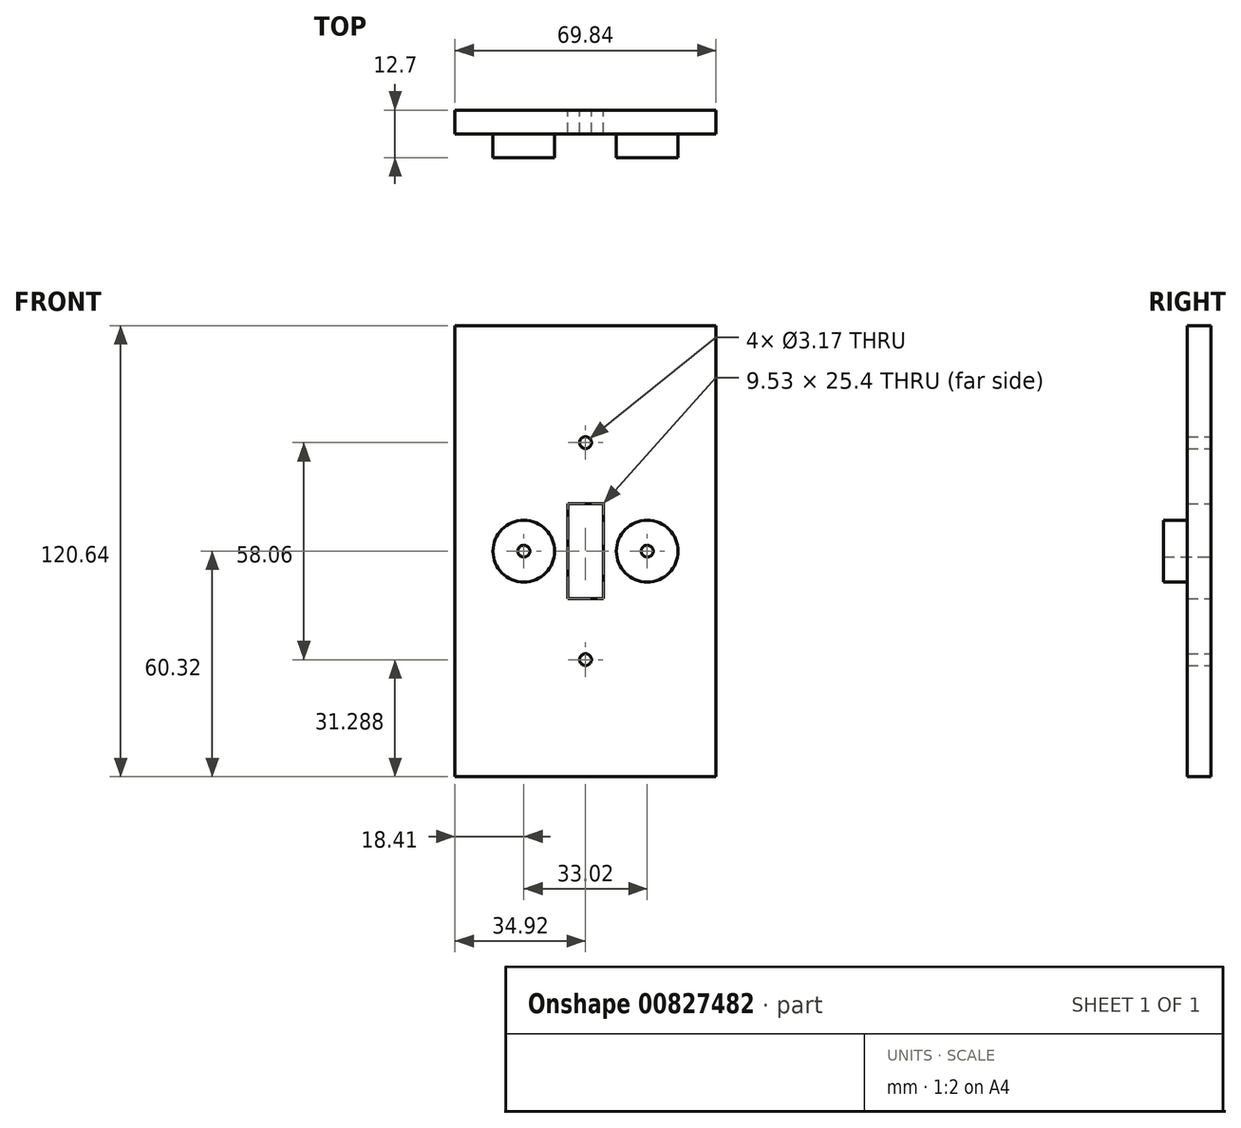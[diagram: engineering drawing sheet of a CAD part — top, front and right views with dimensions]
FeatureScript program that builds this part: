
annotation { "Feature Type Name" : "Feature", "Feature Type Description" : "" }
export const myFeature = defineFeature(function(context is Context, id is Id, definition is map)
    precondition{}
    {
        {
            var Q0;
            Q0=qCreatedBy(makeId("Front.planeOp"),FACE);
            var sketch = newSketch(context, id + "F0", { "sketchPlane" : qUnion([Q0])});
            skLineSegment(sketch, "E0.bottom", {"start": v(34.92, -60.32) * mm, "end": v(-34.93, -60.33) * mm});
            skLineSegment(sketch, "E0.top", {"start": v(34.93, 60.33) * mm, "end": v(-34.92, 60.32) * mm});
            skLineSegment(sketch, "E0.left", {"start": v(34.92, -60.32) * mm, "end": v(34.93, 60.33) * mm});
            skLineSegment(sketch, "E0.right", {"start": v(-34.93, -60.33) * mm, "end": v(-34.92, 60.32) * mm});
            skPoint(sketch, "E0.middle", {"position": v(0, 0) * mm});
            skLineSegment(sketch, "E1.bottom", {"start": v(4.76, -12.7) * mm, "end": v(-4.76, -12.7) * mm});
            skLineSegment(sketch, "E1.top", {"start": v(4.76, 12.7) * mm, "end": v(-4.76, 12.7) * mm});
            skLineSegment(sketch, "E1.left", {"start": v(4.76, -12.7) * mm, "end": v(4.76, 12.7) * mm});
            skLineSegment(sketch, "E1.right", {"start": v(-4.76, -12.7) * mm, "end": v(-4.76, 12.7) * mm});
            skCircle(sketch, "E2", {"center": v(0, 29.03) * mm, "radius": 1.59 * mm});
            skCircle(sketch, "E3", {"center": v(0, -29.03) * mm, "radius": 1.59 * mm});
            skPoint(sketch, "E3.centerSnap0", {"position": v(0, -12.7) * mm});
            skCircle(sketch, "E4", {"center": v(16.51, 0) * mm, "radius": 1.59 * mm});
            skCircle(sketch, "E5", {"center": v(-16.51, 0) * mm, "radius": 1.59 * mm});
            skCircle(sketch, "E6", {"center": v(-16.51, 0) * mm, "radius": 8.26 * mm});
            skCircle(sketch, "E7", {"center": v(16.51, 0) * mm, "radius": 8.26 * mm});
            skSolve(sketch);
        }
        {
            var Q0;
            Q0=makeQuery(id+"F0.imprint","IMPRINT",FACE,{"disambiguationData":[TD([[makeQuery(id+"F0.imprint","IMPRINT",EDGE,{"derivedFrom":sQuery(id+"F0.wireOp",EDGE,"E0.bottom")}),-1.0]])]});
            extrude(context, id + "F1", {"entities" : qUnion([Q0]), "depth" : 6.35 * mm, "offsetDistance" : 25.4 * mm});
        }
        {
            var Q0;
            Q0=makeQuery(id+"F0.imprint","IMPRINT",FACE,{"disambiguationData":[TD([[makeQuery(id+"F0.imprint","IMPRINT",EDGE,{"derivedFrom":sQuery(id+"F0.wireOp",EDGE,"E5")}),-1.0]])]});
            extrude(context, id + "F2", {"entities" : qUnion([Q0]), "operationType" : NewBodyOperationType.ADD, "depth" : 12.7 * mm, "offsetDistance" : 25.4 * mm});
        }
        {
            var Q0;
            Q0=makeQuery(id+"F0.imprint","IMPRINT",FACE,{"disambiguationData":[TD([[makeQuery(id+"F0.imprint","IMPRINT",EDGE,{"derivedFrom":sQuery(id+"F0.wireOp",EDGE,"E4")}),-1.0]])]});
            extrude(context, id + "F3", {"entities" : qUnion([Q0]), "operationType" : NewBodyOperationType.ADD, "depth" : 12.7 * mm, "offsetDistance" : 25.4 * mm});
        }
    });
